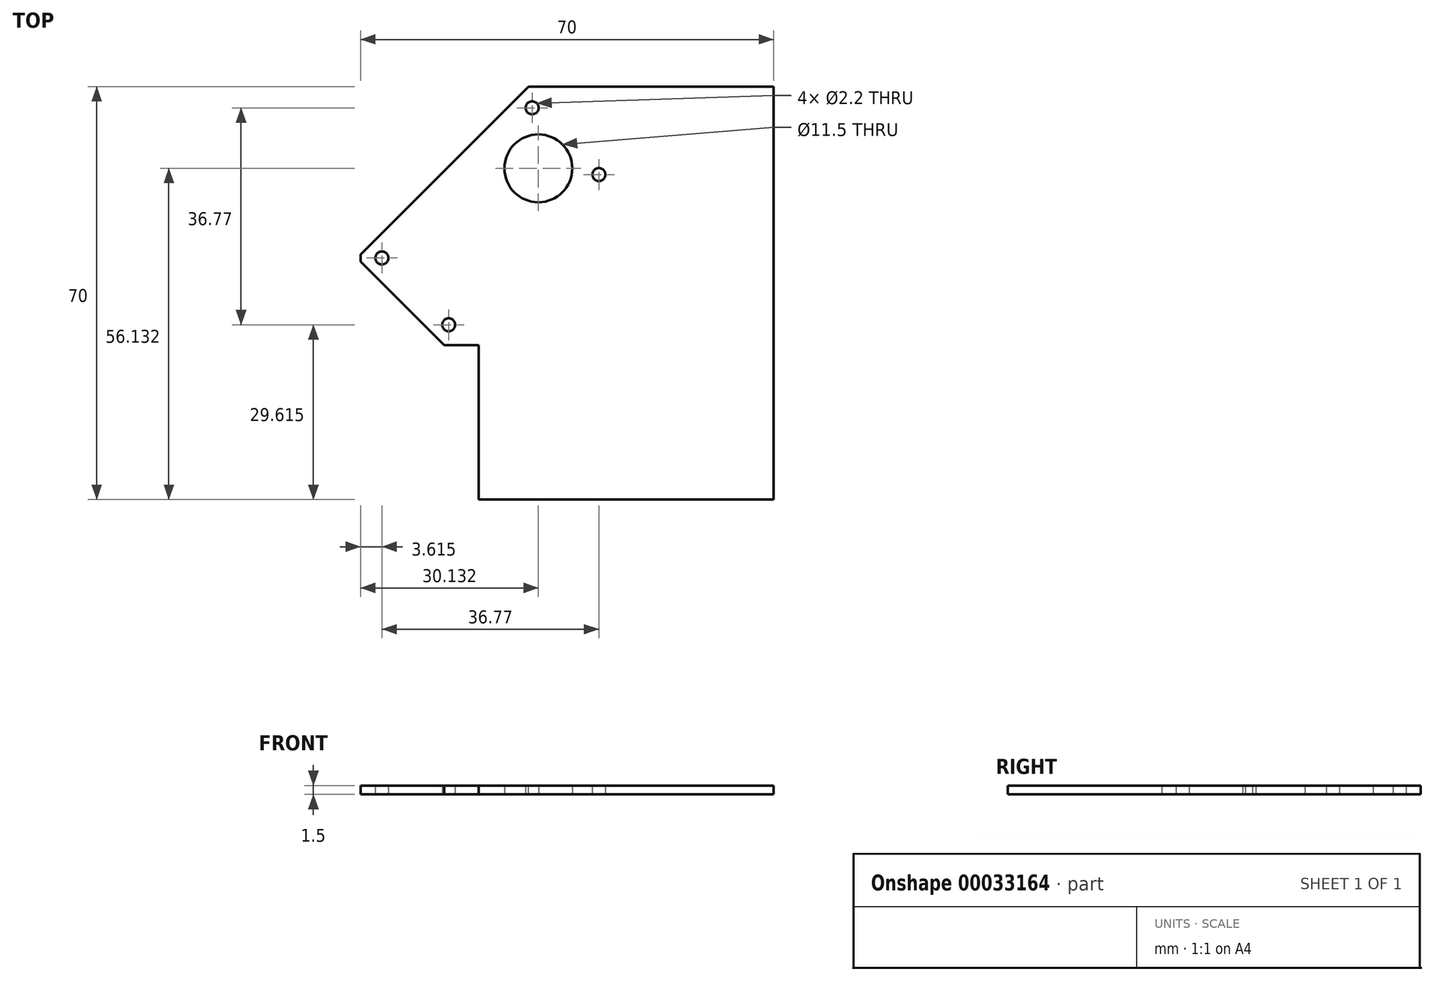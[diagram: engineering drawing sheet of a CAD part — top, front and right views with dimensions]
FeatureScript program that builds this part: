
annotation { "Feature Type Name" : "Feature", "Feature Type Description" : "" }
export const myFeature = defineFeature(function(context is Context, id is Id, definition is map)
    precondition{}
    {
        {
            var Q0;
            Q0=qCreatedBy(makeId("Top.planeOp"),FACE);
            var sketch = newSketch(context, id + "F0", { "sketchPlane" : qUnion([Q0])});
            skLineSegment(sketch, "E0.bottom", {"start": v(-35, 35) * mm, "end": v(35, 35) * mm});
            skLineSegment(sketch, "E0.top", {"start": v(-35, -35) * mm, "end": v(35, -35) * mm});
            skLineSegment(sketch, "E0.left", {"start": v(-35, 35) * mm, "end": v(-35, -35) * mm});
            skLineSegment(sketch, "E0.right", {"start": v(35, 35) * mm, "end": v(35, -35) * mm});
            skPoint(sketch, "E0.middle", {"position": v(0, 0) * mm});
            skLineSegment(sketch, "E1", {"start": v(-25.73, 0.27) * mm, "end": v(-0.27, 25.73) * mm, "construction": true});
            skPoint(sketch, "E2", {"position": v(-13, 13) * mm});
            skLineSegment(sketch, "E3", {"start": v(-25.73, 0.27) * mm, "end": v(-31.38, 5.93) * mm, "construction": true});
            skLineSegment(sketch, "E4", {"start": v(-31.38, 5.93) * mm, "end": v(-5.93, 31.38) * mm, "construction": true});
            skLineSegment(sketch, "E5", {"start": v(-5.93, 31.38) * mm, "end": v(-0.27, 25.73) * mm, "construction": true});
            skLineSegment(sketch, "E6.MirrorCS", {"start": v(-25.73, 0.27) * mm, "end": v(-20.07, -5.38) * mm, "construction": true});
            skLineSegment(sketch, "E7.MirrorCS", {"start": v(-20.07, -5.38) * mm, "end": v(5.38, 20.07) * mm, "construction": true});
            skLineSegment(sketch, "E8.MirrorCS", {"start": v(5.38, 20.07) * mm, "end": v(-0.27, 25.73) * mm, "construction": true});
            skCircle(sketch, "E9", {"center": v(-5.93, 31.38) * mm, "radius": 1.1 * mm});
            skCircle(sketch, "E10", {"center": v(5.38, 20.07) * mm, "radius": 1.1 * mm});
            skCircle(sketch, "E11", {"center": v(-31.38, 5.93) * mm, "radius": 1.1 * mm});
            skCircle(sketch, "E12", {"center": v(-20.07, -5.38) * mm, "radius": 1.1 * mm});
            skCircle(sketch, "E13", {"center": v(-4.87, 21.13) * mm, "radius": 5.75 * mm});
            skSolve(sketch);
        }
        {
            var Q0;
            Q0 = qSketchRegion(id + "F0", true);
            extrude(context, id + "F1", {"entities" : qUnion([Q0]), "depth" : 1.5 * mm});
        }
        {
            var Q0;
            Q0=makeQuery(id+"F1.opExtrude","CAP_FACE",FACE,{"disambiguationData":[OSD([sQuery(id+"F0.wireOp",EDGE,"E0.bottom"),sQuery(id+"F0.wireOp",EDGE,"E0.top"),sQuery(id+"F0.wireOp",EDGE,"E0.left"),sQuery(id+"F0.wireOp",EDGE,"E0.right"),sQuery(id+"F0.wireOp",EDGE,"E9"),sQuery(id+"F0.wireOp",EDGE,"E10"),sQuery(id+"F0.wireOp",EDGE,"E11"),sQuery(id+"F0.wireOp",EDGE,"E12"),sQuery(id+"F0.wireOp",EDGE,"E13")])],"isStart":false});
            var sketch = newSketch(context, id + "F2", { "sketchPlane" : qUnion([Q0])});
            skPoint(sketch, "E14", {"position": v(-5.93, 31.38) * mm});
            skPoint(sketch, "E15", {"position": v(-31.38, 5.93) * mm});
            skLineSegment(sketch, "E16", {"start": v(-35, 6.56) * mm, "end": v(-6.56, 35) * mm});
            skLineSegment(sketch, "E17", {"start": v(-5.93, 31.38) * mm, "end": v(-31.38, 5.93) * mm, "construction": true});
            skPoint(sketch, "E18", {"position": v(-20.07, -5.38) * mm});
            skLineSegment(sketch, "E19", {"start": v(-31.38, 5.93) * mm, "end": v(-20.07, -5.38) * mm, "construction": true});
            skLineSegment(sketch, "E20", {"start": v(-35, 5.3) * mm, "end": v(-20.86, -8.84) * mm});
            skLineSegment(sketch, "E21", {"start": v(-20.86, -8.84) * mm, "end": v(-15, -8.84) * mm});
            skLineSegment(sketch, "E22", {"start": v(-15, -8.84) * mm, "end": v(-15, -35) * mm});
            skSolve(sketch);
        }
        {
            var Q0;
            {var subQ0=sQuery(id+"F2.wireOp",EDGE,"E16");Q0=makeQuery(id+"F2.imprint","IMPRINT",FACE,{"disambiguationData":[TD([[makeQuery(id+"F2.imprint","IMPRINT",EDGE,{"derivedFrom":subQ0}),1.0]])]});}
            var Q1;
            {var subQ0=sQuery(id+"F2.wireOp",EDGE,"E20");Q1=makeQuery(id+"F2.imprint","IMPRINT",FACE,{"disambiguationData":[TD([[makeQuery(id+"F2.imprint","IMPRINT",EDGE,{"derivedFrom":subQ0}),-1.0]])]});}
            extrude(context, id + "F3", {"entities" : qUnion([Q0, Q1]), "operationType" : NewBodyOperationType.REMOVE, "endBound" : BoundingType.UP_TO_NEXT, "oppositeDirection" : true, "depth" : 25 * mm});
        }
    });
